# Revit family: MKT3H-1600(1800,2000)G70A
name_source: partatom
category: Mechanical Equipment
revit_build: Autodesk Revit 2013 (Build: 20120221_2030(x64)
units: mm (PartAtom-declared; Revit-internal decimal feet)

## types (3) — shared parameters
Condensation = water
Depth = 809 mm
Description = High efficiency water cooled
Drain pipe = 32 mm
Height = 400 mm  [stored 1.31234 ft]
Installation = Indoor installation
Liquid pipe = 19.05 mm  [stored 0.0625 ft]
Manufacturer = Midea
Net Weight = 76.00 kg
Power supply = 220-240V ~50Hz
Series = FCU
Width = 1290 mm
clearance access behind = 200 mm  [stored 0.656168 ft]
clearance access left = 500 mm  [stored 1.64042 ft]
clearance access right = 500 mm  [stored 1.64042 ft]
zero-valued in all types: clearance access front

## per-type parameters (varying)
| type | Air Flow(H/M/L) | Cooling Capacity(H/M/L) | Heating Capacity(H/M/L) | Power Input(H/M/L) | Rated current |
| MKT3H-1600G100A | 2272/2126/1911 m3/h | 12.99/12.02/11.04 kW | 14.07/12.91/11.78 kW | 546/475/415 W | 3 A |
| MKT3H-1800G100A | 3177/2983/2327 m3/h | 15.25/13.42/12.38 kW | 18.23/16.84/14.76 kW | 782/683/606 W | 3 A |
| MKT3H-2000G100A | 3411/3034/2588 m3/h | 16.71/15.15/13.58 kW | 19.94/17.26/15.25 kW | 887/755/628 W | 4 A |

note: column(s) folded — value = type name in every type: Model

note: [stored X ft] marks values corroborated as IEEE doubles in the binary element streams (Revit-internal decimal feet)

## geometry (parser evidence)
native form markers: Blend x2, Sweep x4
no freeform markers — native parametric forms only
